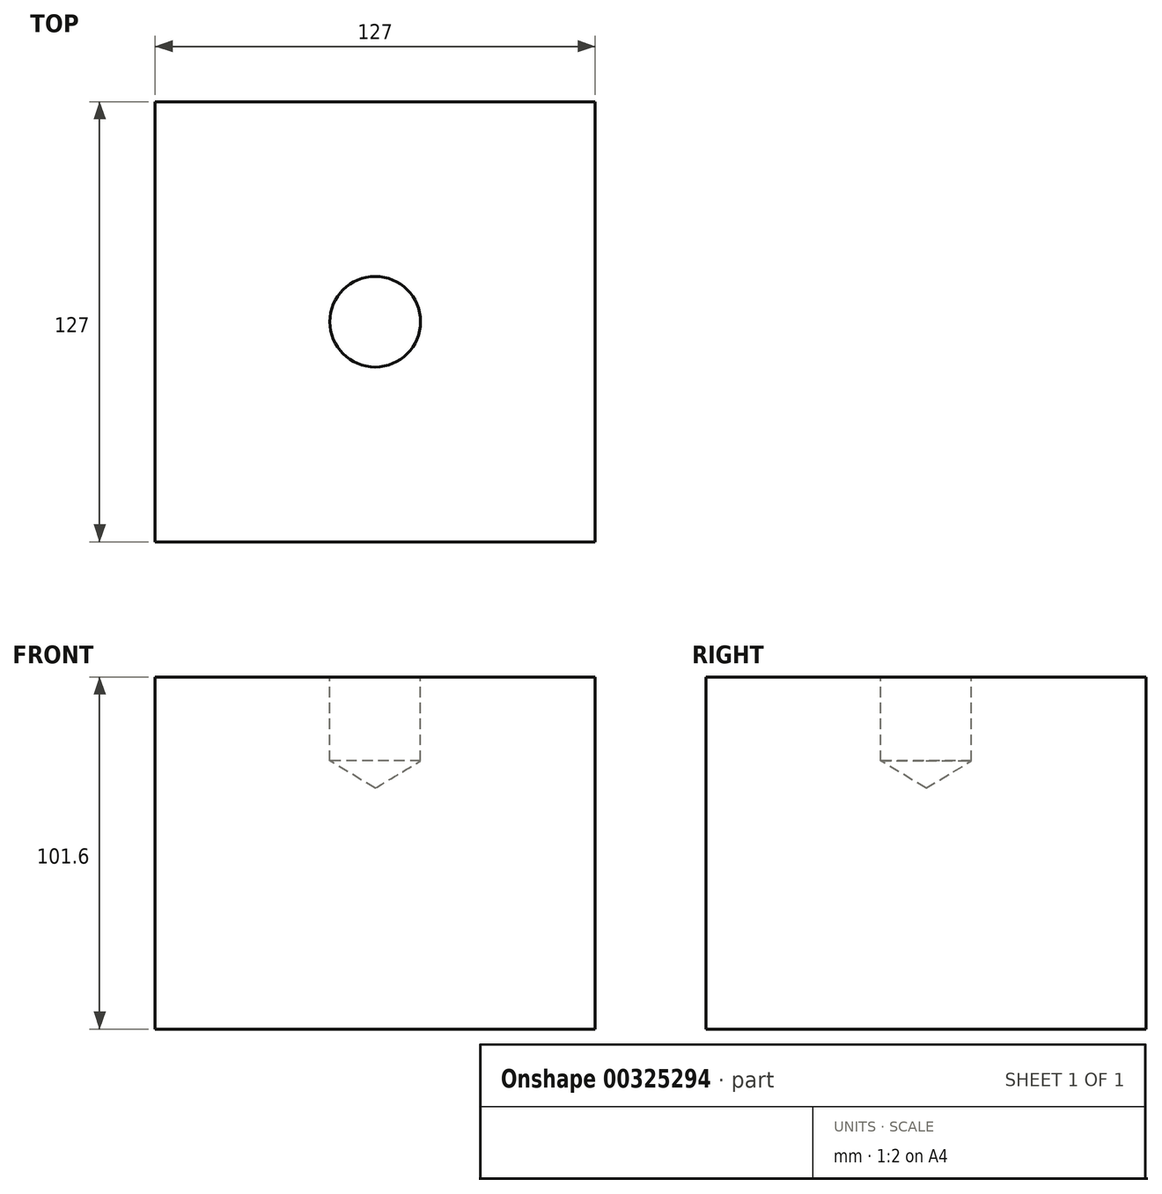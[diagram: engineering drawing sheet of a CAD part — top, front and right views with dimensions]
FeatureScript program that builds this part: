
annotation { "Feature Type Name" : "Feature", "Feature Type Description" : "" }
export const myFeature = defineFeature(function(context is Context, id is Id, definition is map)
    precondition{}
    {
        {
            var Q0;
            Q0=qCreatedBy(makeId("Front.planeOp"),FACE);
            var sketch = newSketch(context, id + "F0", { "sketchPlane" : qUnion([Q0])});
            skLineSegment(sketch, "E0", {"start": v(0, 0) * mm, "end": v(0, 50.8) * mm});
            skLineSegment(sketch, "E1", {"start": v(0, 50.8) * mm, "end": v(-63.5, 50.8) * mm});
            skLineSegment(sketch, "E2", {"start": v(-63.5, 50.8) * mm, "end": v(-63.5, -50.8) * mm});
            skLineSegment(sketch, "E3", {"start": v(-63.5, -50.8) * mm, "end": v(63.5, -50.8) * mm});
            skLineSegment(sketch, "E4", {"start": v(63.5, -50.8) * mm, "end": v(63.5, 50.8) * mm});
            skLineSegment(sketch, "E5", {"start": v(63.5, 50.8) * mm, "end": v(0, 50.8) * mm});
            skSolve(sketch);
        }
        {
            var Q0;
            Q0 = qSketchRegion(id + "F0", true);
            extrude(context, id + "F1", {"entities" : qUnion([Q0]), "endBound" : BoundingType.SYMMETRIC, "depth" : 127 * mm});
        }
        {
            var Q0;
            Q0=makeQuery(id+"F1.opExtrude","SWEPT_FACE",FACE,{"disambiguationData":[OSD([sQuery(id+"F0.wireOp",EDGE,"E1"),sQuery(id+"F0.wireOp",EDGE,"E5")])]});
            var sketch = newSketch(context, id + "F2", { "sketchPlane" : qUnion([Q0])});
            skPoint(sketch, "E6", {"position": v(0, 0) * mm});
            skSolve(sketch);
        }
        {
            var Q0;
            Q0=sQuery(id+"F2.wireOp",VERTEX,"E6");
            var Q1;
            Q1=makeQuery(id+"F1.opExtrude","SWEPT_BODY",BODY,{"disambiguationData":[OSD([sQuery(id+"F0.wireOp",EDGE,"E1"),sQuery(id+"F0.wireOp",EDGE,"E2"),sQuery(id+"F0.wireOp",EDGE,"E3"),sQuery(id+"F0.wireOp",EDGE,"E4"),sQuery(id+"F0.wireOp",EDGE,"E5")])]});
            hole(context, id + "F3", {"style" : HoleStyle.SIMPLE, "endStyle" : HoleEndStyle.BLIND, "holeDiameter" : 26.16 * mm, "holeDepth" : 24.23 * mm, "tappedDepth" : 12.7 * mm, "tapClearance" : 3, "startFromSketch" : true, "locations" : qUnion([Q0]), "scope" : qUnion([Q1])});
        }
    });
